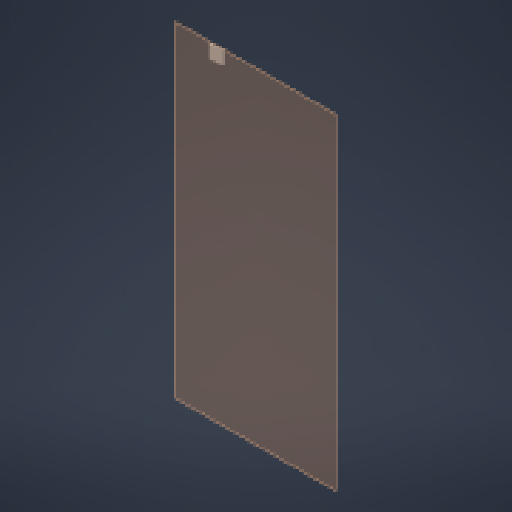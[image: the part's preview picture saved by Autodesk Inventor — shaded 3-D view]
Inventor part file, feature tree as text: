
AUTODESK INVENTOR PART (.ipt)
format: ipt  version: 2024 (Build 280153000, 153)  size: 118,272 bytes
history: native  units: mm
features: other x4, plane x1, sketch x1
ambient origin geometry x8: Origin, YZ Plane, XZ Plane, XY Plane, X Axis, Y Axis, Z Axis, Center Point
feature tree (6):
  plane  "Plano de trabajo1"
  sketch  "Boceto1"  dims[d0=90.0mm d1=30.0mm d2=30.0mm d3=30.0mm d4=30.0mm d5=30.0mm]
  other  "<userpath>\Downloads\Piezas CMR\Marco_APM_001\Marco_apm_001-3.iam"
  other  "Marco_apm_001-3.iam"
  other  "Marco_Conveyor_Aereo:1"
  other  "Marco:1"
